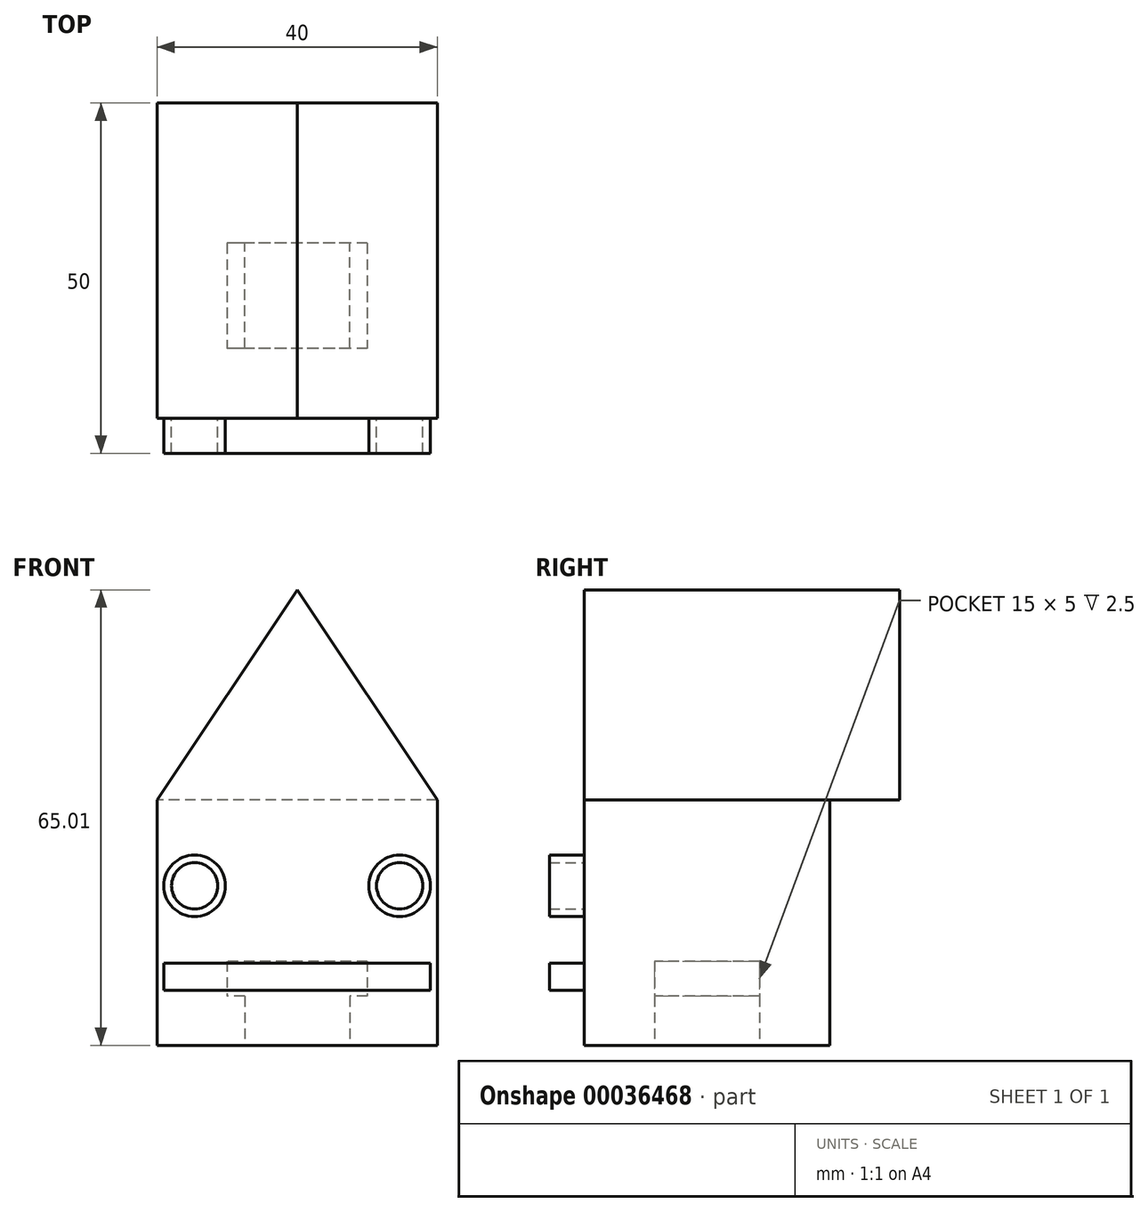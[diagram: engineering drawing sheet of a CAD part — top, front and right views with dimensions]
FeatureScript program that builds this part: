
annotation { "Feature Type Name" : "Feature", "Feature Type Description" : "" }
export const myFeature = defineFeature(function(context is Context, id is Id, definition is map)
    precondition{}
    {
        {
            var Q0;
            Q0=qCreatedBy(makeId("Front.planeOp"),FACE);
            var sketch = newSketch(context, id + "F0", { "sketchPlane" : qUnion([Q0])});
            skLineSegment(sketch, "E0.rect.bottom", {"start": v(20, 17.5) * mm, "end": v(-20, 17.5) * mm});
            skLineSegment(sketch, "E0.rect.top", {"start": v(20, -17.5) * mm, "end": v(-20, -17.5) * mm});
            skLineSegment(sketch, "E0.rect.left", {"start": v(20, 17.5) * mm, "end": v(20, -17.5) * mm});
            skLineSegment(sketch, "E0.rect.right", {"start": v(-20, 17.5) * mm, "end": v(-20, -17.5) * mm});
            skPoint(sketch, "E0.rect.middle", {"position": v(0, 0) * mm});
            skSolve(sketch);
        }
        {
            var Q0;
            Q0 = qSketchRegion(id + "F0", true);
            extrude(context, id + "F1", {"entities" : qUnion([Q0]), "endBound" : BoundingType.SYMMETRIC, "depth" : 35 * mm});
        }
        {
            var Q0;
            Q0=qCreatedBy(makeId("Front.planeOp"),FACE);
            var sketch = newSketch(context, id + "F2", { "sketchPlane" : qUnion([Q0])});
            skLineSegment(sketch, "E1.rect.bottom", {"start": v(7.5, -10.5) * mm, "end": v(-7.5, -10.5) * mm});
            skLineSegment(sketch, "E1.rect.top", {"start": v(7.5, -20.5) * mm, "end": v(-7.5, -20.5) * mm});
            skLineSegment(sketch, "E1.rect.left", {"start": v(7.5, -10.5) * mm, "end": v(7.5, -20.5) * mm});
            skLineSegment(sketch, "E1.rect.right", {"start": v(-7.5, -10.5) * mm, "end": v(-7.5, -20.5) * mm});
            skPoint(sketch, "E1.rect.middle", {"position": v(0, -15.5) * mm});
            skLineSegment(sketch, "E2.rect.bottom", {"start": v(10, -5.5) * mm, "end": v(-10, -5.5) * mm});
            skLineSegment(sketch, "E2.rect.top", {"start": v(10, -10.5) * mm, "end": v(-10, -10.5) * mm});
            skLineSegment(sketch, "E2.rect.left", {"start": v(10, -5.5) * mm, "end": v(10, -10.5) * mm});
            skLineSegment(sketch, "E2.rect.right", {"start": v(-10, -5.5) * mm, "end": v(-10, -10.5) * mm});
            skPoint(sketch, "E2.rect.middle", {"position": v(0, -8) * mm});
            skSolve(sketch);
        }
        {
            var Q0;
            Q0 = qSketchRegion(id + "F2", true);
            extrude(context, id + "F3", {"entities" : qUnion([Q0]), "operationType" : NewBodyOperationType.REMOVE, "endBound" : BoundingType.SYMMETRIC, "oppositeDirection" : true, "depth" : 15 * mm});
        }
        {
            var Q0;
            Q0=makeQuery(id+"F1.opExtrude","CAP_FACE",FACE,{"disambiguationData":[OSD([sQuery(id+"F0.wireOp",EDGE,"E0.rect.bottom"),sQuery(id+"F0.wireOp",EDGE,"E0.rect.top"),sQuery(id+"F0.wireOp",EDGE,"E0.rect.left"),sQuery(id+"F0.wireOp",EDGE,"E0.rect.right")])],"isStart":false});
            var sketch = newSketch(context, id + "F4", { "sketchPlane" : qUnion([Q0])});
            skCircle(sketch, "E3", {"center": v(-14.63, 5.27) * mm, "radius": 4.4 * mm});
            skCircle(sketch, "E4", {"center": v(14.63, 5.27) * mm, "radius": 4.4 * mm});
            skLineSegment(sketch, "E5", {"start": v(0, 17.88) * mm, "end": v(0, -18.04) * mm, "construction": true});
            skLineSegment(sketch, "E6.rect.bottom", {"start": v(19, -9.66) * mm, "end": v(-19, -9.66) * mm});
            skLineSegment(sketch, "E6.rect.top", {"start": v(19, -5.8) * mm, "end": v(-19, -5.8) * mm});
            skLineSegment(sketch, "E6.rect.left", {"start": v(19, -9.66) * mm, "end": v(19, -5.8) * mm});
            skLineSegment(sketch, "E6.rect.right", {"start": v(-19, -9.66) * mm, "end": v(-19, -5.8) * mm});
            skPoint(sketch, "E6.rect.middle", {"position": v(0, -7.73) * mm});
            skCircle(sketch, "E7", {"center": v(-14.63, 5.27) * mm, "radius": 3.3 * mm});
            skCircle(sketch, "E8", {"center": v(14.63, 5.27) * mm, "radius": 3.3 * mm});
            skCircle(sketch, "E9", {"center": v(-14.63, 5.27) * mm, "radius": 2.5 * mm});
            skCircle(sketch, "E10", {"center": v(-14.63, 5.27) * mm, "radius": 1.63 * mm});
            skCircle(sketch, "E11", {"center": v(14.63, 5.27) * mm, "radius": 2.5 * mm});
            skCircle(sketch, "E12", {"center": v(14.63, 5.27) * mm, "radius": 1.63 * mm});
            skLineSegment(sketch, "E13", {"start": v(-20, 17.5) * mm, "end": v(0, 47.5) * mm});
            skLineSegment(sketch, "E14", {"start": v(0, 47.5) * mm, "end": v(20, 17.5) * mm});
            skSolve(sketch);
        }
        {
            var Q0;
            Q0=makeQuery(id+"F4.imprint","IMPRINT",FACE,{"disambiguationData":[TD([[makeQuery(id+"F4.imprint","IMPRINT",EDGE,{"derivedFrom":sQuery(id+"F4.wireOp",EDGE,"E3")}),1.0]])]});
            var Q1;
            Q1=makeQuery(id+"F4.imprint","IMPRINT",FACE,{"disambiguationData":[TD([[makeQuery(id+"F4.imprint","IMPRINT",EDGE,{"derivedFrom":sQuery(id+"F4.wireOp",EDGE,"E4")}),1.0]])]});
            var Q2;
            Q2=makeQuery(id+"F4.imprint","IMPRINT",FACE,{"disambiguationData":[TD([[makeQuery(id+"F4.imprint","IMPRINT",EDGE,{"derivedFrom":sQuery(id+"F4.wireOp",EDGE,"E6.rect.bottom")}),-1.0]])]});
            extrude(context, id + "F5", {"entities" : qUnion([Q0, Q1, Q2]), "operationType" : NewBodyOperationType.ADD, "depth" : 5 * mm});
        }
        {
            var Q0;
            Q0=sQuery(id+"F4.wireOp",EDGE,"E7");
            var Q1;
            Q1=sQuery(id+"F4.wireOp",EDGE,"E8");
            extrude(context, id + "F6", {"bodyType" : ToolBodyType.SURFACE, "surfaceEntities" : qUnion([Q0, Q1]), "depth" : 10 * mm});
        }
        {
            var Q0;
            Q0=sQuery(id+"F4.wireOp",EDGE,"E9");
            var Q1;
            Q1=sQuery(id+"F4.wireOp",EDGE,"E11");
            extrude(context, id + "F7", {"bodyType" : ToolBodyType.SURFACE, "surfaceEntities" : qUnion([Q0, Q1]), "depth" : 15 * mm});
        }
        {
            var Q0;
            Q0=sQuery(id+"F4.wireOp",EDGE,"E10");
            var Q1;
            Q1=sQuery(id+"F4.wireOp",EDGE,"E12");
            extrude(context, id + "F8", {"bodyType" : ToolBodyType.SURFACE, "surfaceEntities" : qUnion([Q0, Q1]), "depth" : 20 * mm});
        }
        {
            var Q0;
            Q0=makeQuery(id+"F4.imprint","IMPRINT",FACE,{"disambiguationData":[TD([[makeQuery(id+"F4.imprint","IMPRINT",EDGE,{"derivedFrom":sQuery(id+"F4.wireOp",EDGE,"E13")}),-1.0]])]});
            extrude(context, id + "F9", {"entities" : qUnion([Q0]), "operationType" : NewBodyOperationType.ADD, "oppositeDirection" : true, "depth" : 45 * mm});
        }
    });
